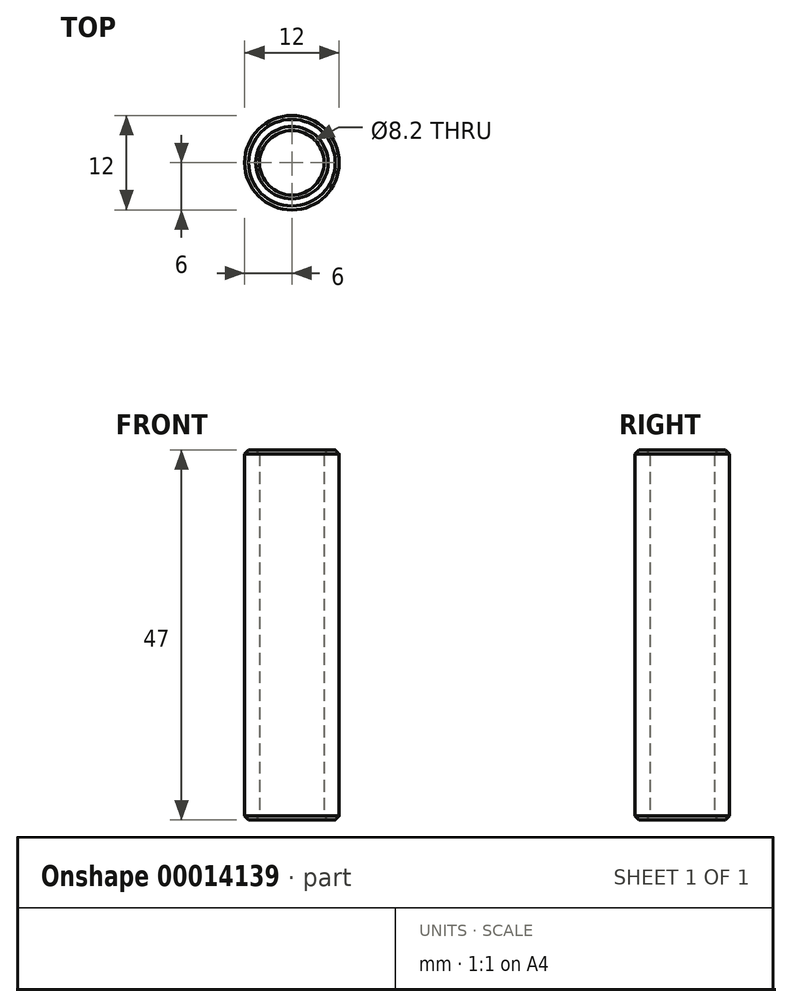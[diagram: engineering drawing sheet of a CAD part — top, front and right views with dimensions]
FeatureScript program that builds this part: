
annotation { "Feature Type Name" : "Feature", "Feature Type Description" : "" }
export const myFeature = defineFeature(function(context is Context, id is Id, definition is map)
    precondition{}
    {
        {
            var Q0;
            Q0=qCreatedBy(makeId("Top.planeOp"),FACE);
            var sketch = newSketch(context, id + "F0", { "sketchPlane" : qUnion([Q0])});
            skCircle(sketch, "E0", {"center": v(0, 0) * mm, "radius": 6 * mm});
            skCircle(sketch, "E1", {"center": v(0, 0) * mm, "radius": 4.1 * mm});
            skSolve(sketch);
        }
        {
            var Q0;
            Q0 = qSketchRegion(id + "F0", true);
            extrude(context, id + "F1", {"entities" : qUnion([Q0]), "depth" : 47 * mm});
        }
        {
            var Q0;
            Q0=makeQuery(id+"F1.opExtrude","CAP_FACE",FACE,{"disambiguationData":[OSD([sQuery(id+"F0.wireOp",EDGE,"E0"),sQuery(id+"F0.wireOp",EDGE,"E1")])],"isStart":true});
            var Q1;
            Q1=makeQuery(id+"F1.opExtrude","CAP_FACE",FACE,{"disambiguationData":[OSD([sQuery(id+"F0.wireOp",EDGE,"E0"),sQuery(id+"F0.wireOp",EDGE,"E1")])],"isStart":false});
            chamfer(context, id + "F2", {"entities" : qUnion([Q0, Q1]), "width" : .5 * mm, "tangentPropagation" : true});
        }
    });
